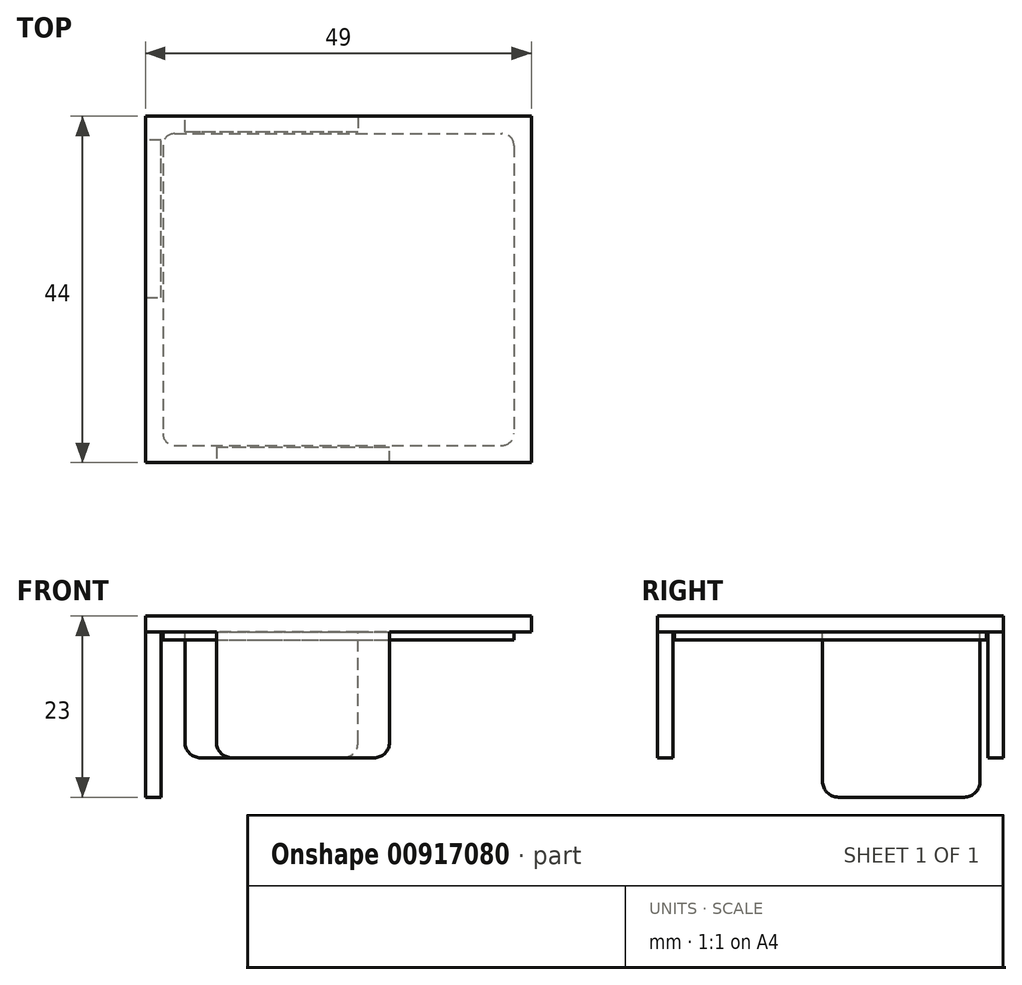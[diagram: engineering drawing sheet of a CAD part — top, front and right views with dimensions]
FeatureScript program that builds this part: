
annotation { "Feature Type Name" : "Feature", "Feature Type Description" : "" }
export const myFeature = defineFeature(function(context is Context, id is Id, definition is map)
    precondition{}
    {
        {
            var Q0;
            Q0=qCreatedBy(makeId("Top.planeOp"),FACE);
            var sketch = newSketch(context, id + "F0", { "sketchPlane" : qUnion([Q0])});
            skLineSegment(sketch, "E0.bottom", {"start": v(49, 0) * mm, "end": v(0, 0) * mm});
            skLineSegment(sketch, "E0.top", {"start": v(49, 44) * mm, "end": v(0, 44) * mm});
            skLineSegment(sketch, "E0.left", {"start": v(49, 0) * mm, "end": v(49, 44) * mm});
            skLineSegment(sketch, "E0.right", {"start": v(0, 0) * mm, "end": v(0, 44) * mm});
            skLineSegment(sketch, "E1", {"start": v(0, 0) * mm, "end": v(9, 0) * mm});
            skLineSegment(sketch, "E2", {"start": v(9, 2) * mm, "end": v(31, 2) * mm});
            skLineSegment(sketch, "E3", {"start": v(9, 0) * mm, "end": v(31, 0) * mm});
            skLineSegment(sketch, "E4", {"start": v(31, 0) * mm, "end": v(31, 2) * mm});
            skLineSegment(sketch, "E5", {"start": v(9, 2) * mm, "end": v(9, 0) * mm});
            skLineSegment(sketch, "E6", {"start": v(0, 44) * mm, "end": v(5, 44) * mm});
            skLineSegment(sketch, "E7", {"start": v(5, 44) * mm, "end": v(27, 44) * mm});
            skLineSegment(sketch, "E8", {"start": v(27, 44) * mm, "end": v(27, 42) * mm});
            skLineSegment(sketch, "E9", {"start": v(27, 42) * mm, "end": v(5, 42) * mm});
            skLineSegment(sketch, "E10", {"start": v(5, 42) * mm, "end": v(5, 44) * mm});
            skLineSegment(sketch, "E11", {"start": v(0, 44) * mm, "end": v(0, 41) * mm});
            skLineSegment(sketch, "E12", {"start": v(0, 41) * mm, "end": v(0, 21) * mm});
            skLineSegment(sketch, "E13", {"start": v(0, 21) * mm, "end": v(2, 21) * mm});
            skLineSegment(sketch, "E14", {"start": v(2, 21) * mm, "end": v(2, 41) * mm});
            skLineSegment(sketch, "E15", {"start": v(2, 41) * mm, "end": v(0, 41) * mm});
            skLineSegment(sketch, "E16", {"start": v(0, 44) * mm, "end": v(0, 41.8) * mm});
            skLineSegment(sketch, "E17.bottom", {"start": v(2.2, 41.8) * mm, "end": v(46.8, 41.8) * mm});
            skLineSegment(sketch, "E17.top", {"start": v(2.2, 2.2) * mm, "end": v(46.8, 2.2) * mm});
            skLineSegment(sketch, "E17.left", {"start": v(2.2, 41.8) * mm, "end": v(2.2, 2.2) * mm});
            skLineSegment(sketch, "E17.right", {"start": v(46.8, 41.8) * mm, "end": v(46.8, 2.2) * mm});
            skSolve(sketch);
        }
        {
            var Q0;
            {var subQ8=sQuery(id+"F0.wireOp",EDGE,"E0.left");Q0=makeQuery(id+"F0.imprint","IMPRINT",FACE,{"disambiguationData":[TD([[makeQuery(id+"F0.imprint","IMPRINT",EDGE,{"derivedFrom":subQ8}),1.0]])]});}
            extrude(context, id + "F1", {"entities" : qUnion([Q0]), "oppositeDirection" : true, "depth" : 2 * mm, "offsetDistance" : 25.4 * mm});
        }
        {
            var Q0;
            {var subQ0=sQuery(id+"F0.wireOp",EDGE,"E8");Q0=makeQuery(id+"F0.imprint","IMPRINT",FACE,{"disambiguationData":[TD([[makeQuery(id+"F0.imprint","IMPRINT",EDGE,{"derivedFrom":subQ0}),-1.0]])]});}
            var Q1;
            Q1=makeQuery(id+"F0.imprint","IMPRINT",FACE,{"disambiguationData":[TD([[makeQuery(id+"F0.imprint","IMPRINT",EDGE,{"derivedFrom":sQuery(id+"F0.wireOp",EDGE,"E2")}),-1.0]])]});
            extrude(context, id + "F2", {"entities" : qUnion([Q0, Q1]), "operationType" : NewBodyOperationType.ADD, "oppositeDirection" : true, "depth" : 18 * mm, "offsetDistance" : 25 * mm});
        }
        {
            var Q0;
            {var subQ0=sQuery(id+"F0.wireOp",EDGE,"E13");Q0=makeQuery(id+"F0.imprint","IMPRINT",FACE,{"disambiguationData":[TD([[makeQuery(id+"F0.imprint","IMPRINT",EDGE,{"derivedFrom":subQ0}),1.0]])]});}
            extrude(context, id + "F3", {"entities" : qUnion([Q0]), "operationType" : NewBodyOperationType.ADD, "oppositeDirection" : true, "depth" : 23 * mm, "offsetDistance" : 25 * mm});
        }
        {
            var Q0;
            Q0=makeQuery(id+"F0.imprint","IMPRINT",FACE,{"disambiguationData":[TD([[makeQuery(id+"F0.imprint","IMPRINT",EDGE,{"derivedFrom":sQuery(id+"F0.wireOp",EDGE,"E17.bottom")}),-1.0]])]});
            extrude(context, id + "F4", {"entities" : qUnion([Q0]), "operationType" : NewBodyOperationType.ADD, "oppositeDirection" : true, "depth" : 3 * mm, "offsetDistance" : 25 * mm});
        }
        {
            var Q0;
            Q0=makeQuery(id+"F4.opExtrude","SWEPT_EDGE",EDGE,{"disambiguationData":[OSD([sQuery(id+"F0.wireOp",EDGE,"E17.top"),sQuery(id+"F0.wireOp",EDGE,"E17.left")])]});
            var Q1;
            Q1=makeQuery(id+"F4.opExtrude","SWEPT_EDGE",EDGE,{"disambiguationData":[OSD([sQuery(id+"F0.wireOp",EDGE,"E17.bottom"),sQuery(id+"F0.wireOp",EDGE,"E17.left")])]});
            var Q2;
            Q2=makeQuery(id+"F4.opExtrude","SWEPT_EDGE",EDGE,{"disambiguationData":[OSD([sQuery(id+"F0.wireOp",EDGE,"E17.top"),sQuery(id+"F0.wireOp",EDGE,"E17.right")])]});
            var Q3;
            Q3=makeQuery(id+"F4.opExtrude","SWEPT_EDGE",EDGE,{"disambiguationData":[OSD([sQuery(id+"F0.wireOp",EDGE,"E17.bottom"),sQuery(id+"F0.wireOp",EDGE,"E17.right")])]});
            fillet(context, id + "F5", {"entities" : qUnion([Q0, Q1, Q2, Q3]), "radius" : 1.5 * mm, "tangentPropagation" : true, "allowEdgeOverflow" : false});
        }
        {
            var Q0;
            Q0=makeQuery(id+"F2.opExtrude","CAP_EDGE",EDGE,{"disambiguationData":[OSD([sQuery(id+"F0.wireOp",EDGE,"E10")])],"isStart":false});
            var Q1;
            Q1=makeQuery(id+"F2.opExtrude","CAP_EDGE",EDGE,{"disambiguationData":[OSD([sQuery(id+"F0.wireOp",EDGE,"E8")])],"isStart":false});
            var Q2;
            Q2=makeQuery(id+"F3.opExtrude","CAP_EDGE",EDGE,{"disambiguationData":[OSD([sQuery(id+"F0.wireOp",EDGE,"E15")])],"isStart":false});
            var Q3;
            Q3=makeQuery(id+"F3.opExtrude","CAP_EDGE",EDGE,{"disambiguationData":[OSD([sQuery(id+"F0.wireOp",EDGE,"E13")])],"isStart":false});
            var Q4;
            Q4=makeQuery(id+"F2.opExtrude","CAP_EDGE",EDGE,{"disambiguationData":[OSD([sQuery(id+"F0.wireOp",EDGE,"E4")])],"isStart":false});
            var Q5;
            Q5=makeQuery(id+"F2.opExtrude","CAP_EDGE",EDGE,{"disambiguationData":[OSD([sQuery(id+"F0.wireOp",EDGE,"E5")])],"isStart":false});
            fillet(context, id + "F6", {"entities" : qUnion([Q0, Q1, Q2, Q3, Q4, Q5]), "radius" : 2 * mm, "tangentPropagation" : true, "allowEdgeOverflow" : false});
        }
    });
